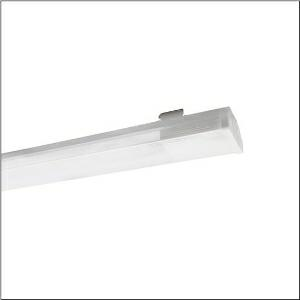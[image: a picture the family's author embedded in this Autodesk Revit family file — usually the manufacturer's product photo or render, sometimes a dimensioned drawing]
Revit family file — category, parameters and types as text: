
# Revit family: modario_31_gen_2_53bm8127u4l3d2_3fb6
name_source: partatom
category: Lighting Fixtures
units: mm (PartAtom-declared; Revit-internal decimal feet)

## family parameters
Cut with Voids When Loaded = No
Host = Face
Light Source = No
Part Type = Normal
Room Calculation Point = No
Round Connector Dimension = Use Diameter
Shared = No

## types (1)
- Modario 31 Gen.2 (1 x LED, 23600 lm, 126 W, 4000K)
    Apparent Load = 126 VA
    CIE Flux Codes = 47 80 95 93 100
    Color Rendering = 80
    Color Temperature = 4000K
    Default Elevation = 1800 mm
    Description = Modario 31 Gen.2, luminaire insert, of sheet steel, coil coated, white, length: 2.392mm, width: 81mm, height: 82mm, 8x system unit, system units: 299mm, LED rated luminous flux: 23.600lm, light colour: 840, SDCM (Standard Deviation of Colour Matching)MacAdam ≤ 3 SDCM (initial), control gear: ON/OFF, with plug, 3-pole, with phase selection, mains connection: 220..240V, AC, 50/60Hz, rated input power: 126W, through-wiring accessed according to module size, primary optical cover: cover, of PMMA, light emission: direct distribution, primary light characteristic: symmetric, protection rating (complete): IP20, protection rating (LED compartment): IP50, insulation class (complete): insulation class I (protective earthing), certification: CE, ENEC, VDE, UKCA, impact resistance: IK03, permissible ambient temperature for indoor applications: -40..+35°C, corresponds to IFS (International Featured Standards) requirements for safety and quality in the food industry, reducing of maximum allowable ambient temperature of 5°C with ceiling mounting, IP40 when using the optional accessory 5TP9018, packaging unit: 1 piece
    Height = 92 mm
    Lamp = 1 x LED
    Lamp Light Flux = 23600 lm
    Lamp Power = 126 W
    Lamp count = 1
    Length = 2392 mm
    Luminous efficacy = 187 lm/W
    Manufacturer = Siteco
    ModVariant = No
    Model = 53BM8127U4L3D2
    Mounting Place = Ceiling
    Mounting Type = Pendant
    Number of Poles = 1
    OnlyDefault = Yes
    Power Factor = 1
    Product Name = Modario 31 Gen.2
    Product group = luminaire insert | ceiling pendant
    ProductGroupID = 901
    Protection Class = Protection class I
    Protection Degree = IP 20
    RLX_Detail_Level = 1
    RLX_Emergency_Light_Flux = 0 lm
    RLX_Emergency_Type = 0
    RLX_Emergency_Type_DB = No
    RlxData = <blob elided: 34745 chars, md5=5e40bf44>
    Socket = socket
    Standby Power = 0 W
    System Light Flux = 23600 lm
    System Power = 126 W
    Type Comments = Product without accessories
    Type Image = l_1341883.jpg
    URL = http://relux.com
    VarID = ---
    Voltage = 0 V
    Weight = 0.00 kg
    Width = 81 mm

## geometry (parser evidence)
native form markers: Blend x4, Sweep x11
no freeform markers — native parametric forms only
